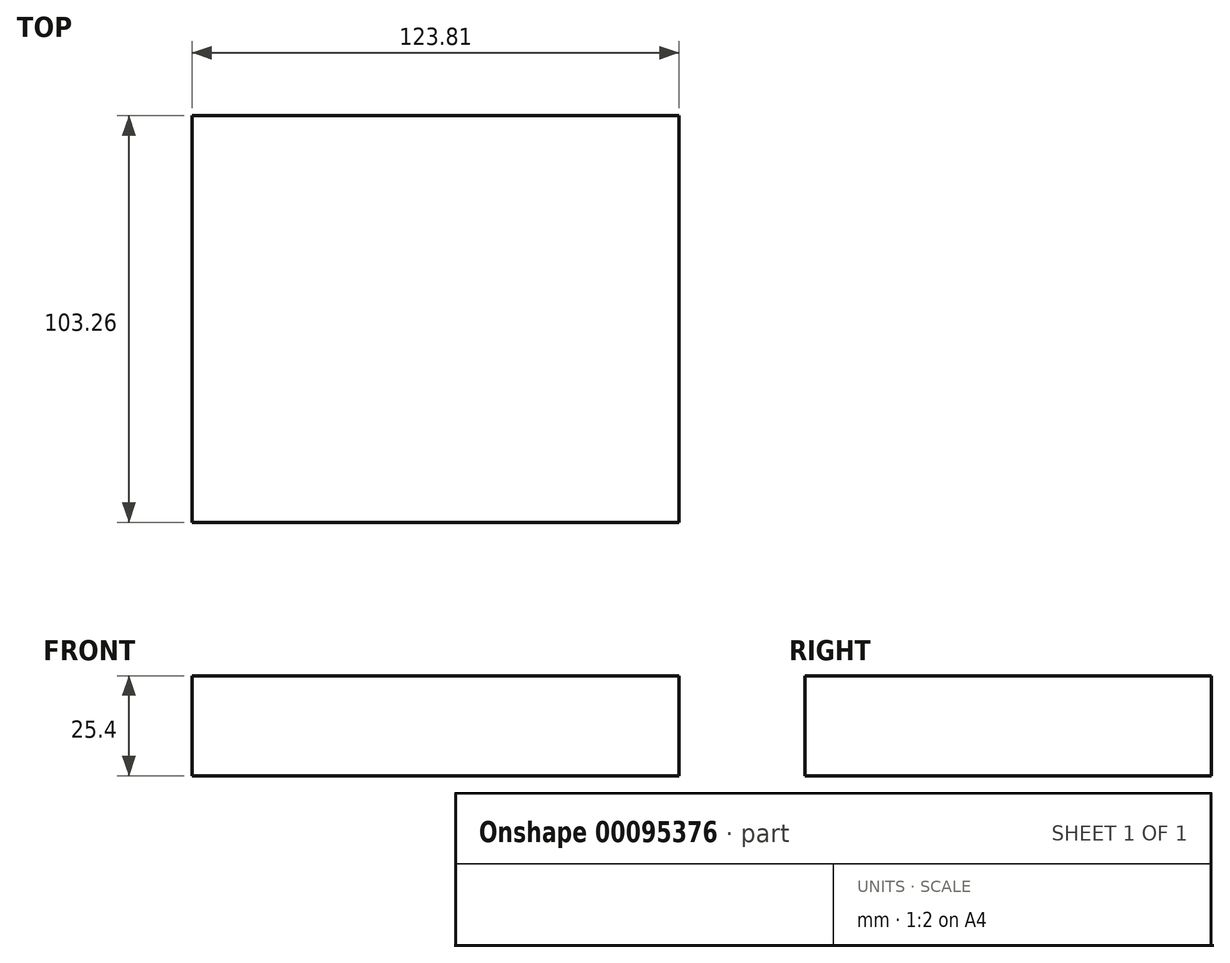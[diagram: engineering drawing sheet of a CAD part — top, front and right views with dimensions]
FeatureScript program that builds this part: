
annotation { "Feature Type Name" : "Feature", "Feature Type Description" : "" }
export const myFeature = defineFeature(function(context is Context, id is Id, definition is map)
    precondition{}
    {
        {
            var Q0;
            Q0=qCreatedBy(makeId("Top.planeOp"),FACE);
            var sketch = newSketch(context, id + "F0", { "sketchPlane" : qUnion([Q0])});
            skLineSegment(sketch, "E0.bottom", {"start": v(-71.3, 60) * mm, "end": v(52.52, 60) * mm});
            skLineSegment(sketch, "E0.top", {"start": v(-71.3, -43.26) * mm, "end": v(52.52, -43.26) * mm});
            skLineSegment(sketch, "E0.left", {"start": v(-71.3, 60) * mm, "end": v(-71.3, -43.26) * mm});
            skLineSegment(sketch, "E0.right", {"start": v(52.52, 60) * mm, "end": v(52.52, -43.26) * mm});
            skSolve(sketch);
        }
        {
            var Q0;
            Q0 = qSketchRegion(id + "F0", true);
            extrude(context, id + "F1", {"entities" : qUnion([Q0]), "endBound" : BoundingType.SYMMETRIC, "depth" : 25.4 * mm});
        }
    });
